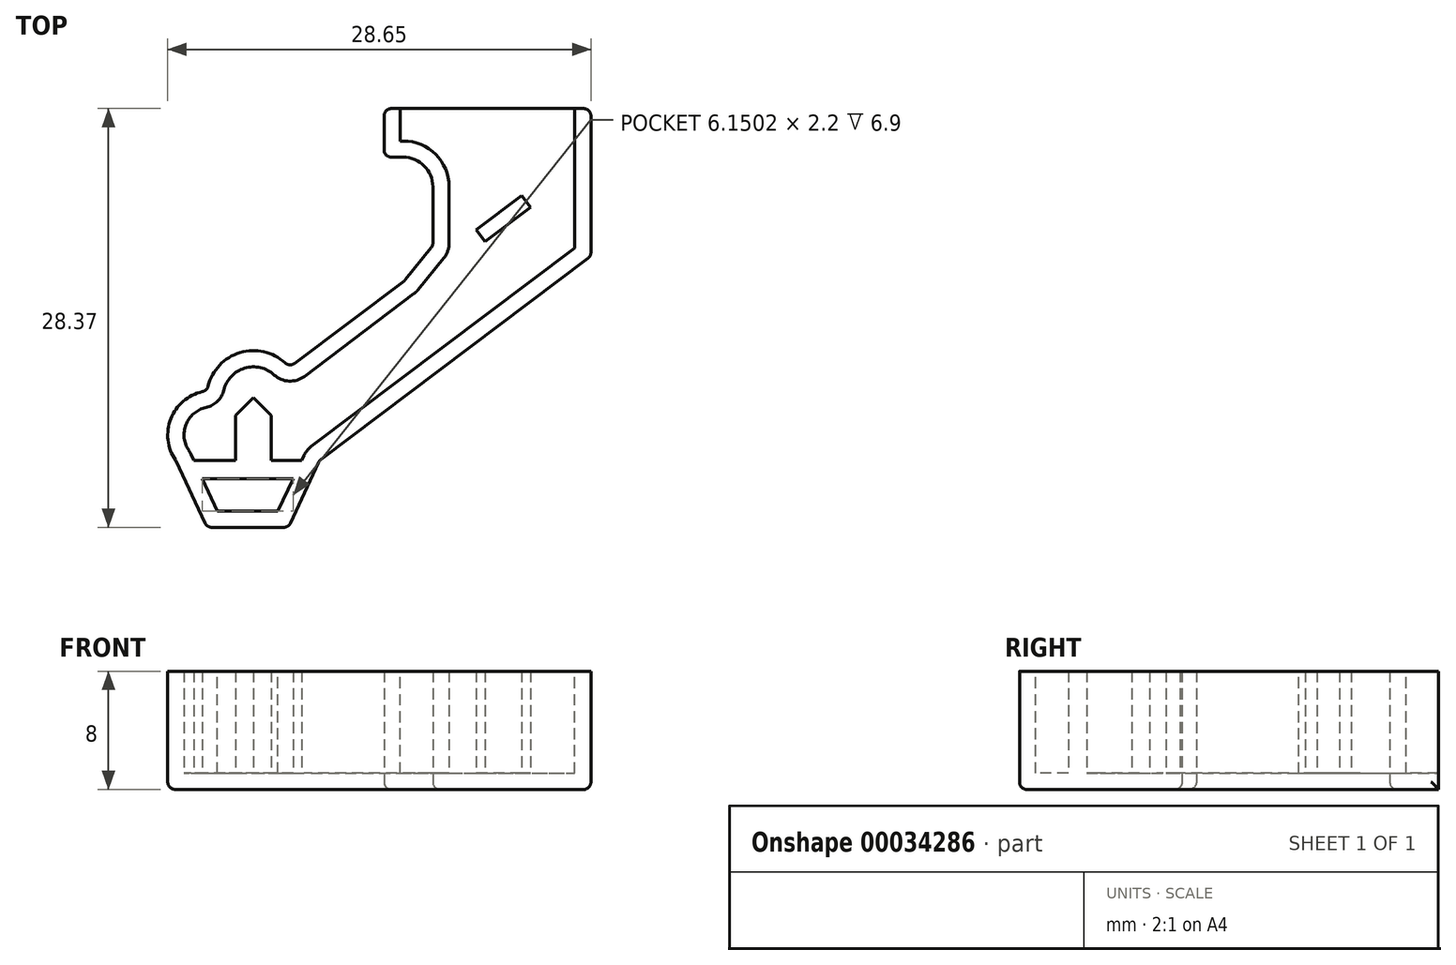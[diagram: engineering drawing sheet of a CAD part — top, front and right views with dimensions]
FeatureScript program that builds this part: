
annotation { "Feature Type Name" : "Feature", "Feature Type Description" : "" }
export const myFeature = defineFeature(function(context is Context, id is Id, definition is map)
    precondition{}
    {
        {
            var Q0;
            Q0=qCreatedBy(makeId("Top.planeOp"),FACE);
            var sketch = newSketch(context, id + "F0", { "sketchPlane" : qUnion([Q0])});
            skLineSegment(sketch, "E0", {"start": v(-14, 0) * mm, "end": v(0, 0) * mm});
            skLineSegment(sketch, "E1", {"start": v(0, 0) * mm, "end": v(0, -10) * mm});
            skLineSegment(sketch, "E2", {"start": v(0, -10) * mm, "end": v(-18.37, -23.84) * mm});
            skLineSegment(sketch, "E3", {"start": v(-18.37, -23.84) * mm, "end": v(-20.48, -28.37) * mm});
            skLineSegment(sketch, "E4", {"start": v(-20.48, -28.37) * mm, "end": v(-25.98, -28.37) * mm});
            skLineSegment(sketch, "E5", {"start": v(-25.98, -28.37) * mm, "end": v(-28.1, -23.84) * mm});
            skLineSegment(sketch, "E6", {"start": v(-14, 0) * mm, "end": v(-14, -3.3) * mm});
            skLineSegment(sketch, "E7", {"start": v(-14, -3.3) * mm, "end": v(-12.7, -3.3) * mm});
            skLineSegment(sketch, "E8", {"start": v(-10.7, -5.3) * mm, "end": v(-10.7, -9.3) * mm});
            skLineSegment(sketch, "E9", {"start": v(-10.7, -9.3) * mm, "end": v(-12.59, -11.63) * mm});
            skLineSegment(sketch, "E10", {"start": v(-12.59, -11.63) * mm, "end": v(-20.41, -17.53) * mm});
            skArc(sketch, "E11", {"start": v(-20.41, -17.53) * mm, "mid": v(-23.72, -16.52) * mm, "end": v(-25.98, -19.13) * mm});
            skArc(sketch, "E12", {"start": v(-25.98, -19.13) * mm, "mid": v(-28.39, -20.88) * mm, "end": v(-28.1, -23.84) * mm});
            skLineSegment(sketch, "E13", {"start": v(-25.98, -19.13) * mm, "end": v(-20.41, -17.53) * mm, "construction": true});
            skLineSegment(sketch, "E14", {"start": v(-25.98, -19.13) * mm, "end": v(-28.1, -23.84) * mm, "construction": true});
            skLineSegment(sketch, "E15", {"start": v(-25.98, -19.13) * mm, "end": v(-25.98, -28.37) * mm, "construction": true});
            skPoint(sketch, "E16.visualSharp", {"position": v(-10.7, -3.3) * mm});
            skArc(sketch, "E16.filletArc", {"start": v(-10.7, -5.3) * mm, "mid": v(-11.29, -3.89) * mm, "end": v(-12.7, -3.3) * mm});
            skSolve(sketch);
        }
        {
            var Q0;
            Q0 = qSketchRegion(id + "F0", true);
            extrude(context, id + "F1", {"entities" : qUnion([Q0]), "depth" : 8 * mm});
        }
        {
            var Q0;
            Q0=makeQuery(id+"F1.opExtrude","SWEPT_EDGE",EDGE,{"disambiguationData":[OSD([sQuery(id+"F0.wireOp",EDGE,"E6"),sQuery(id+"F0.wireOp",EDGE,"E7")])]});
            var Q1;
            Q1=makeQuery(id+"F1.opExtrude","SWEPT_EDGE",EDGE,{"disambiguationData":[OSD([sQuery(id+"F0.wireOp",EDGE,"E8"),sQuery(id+"F0.wireOp",EDGE,"E9")])]});
            var Q2;
            Q2=makeQuery(id+"F1.opExtrude","SWEPT_EDGE",EDGE,{"disambiguationData":[OSD([sQuery(id+"F0.wireOp",EDGE,"E9"),sQuery(id+"F0.wireOp",EDGE,"E10")])]});
            var Q3;
            Q3=makeQuery(id+"F1.opExtrude","SWEPT_EDGE",EDGE,{"disambiguationData":[OSD([sQuery(id+"F0.wireOp",EDGE,"E10"),sQuery(id+"F0.wireOp",EDGE,"E11")])]});
            var Q4;
            Q4=makeQuery(id+"F1.opExtrude","SWEPT_EDGE",EDGE,{"disambiguationData":[OSD([sQuery(id+"F0.wireOp",EDGE,"E11"),sQuery(id+"F0.wireOp",EDGE,"E12")])]});
            var Q5;
            Q5=makeQuery(id+"F1.opExtrude","SWEPT_EDGE",EDGE,{"disambiguationData":[OSD([sQuery(id+"F0.wireOp",EDGE,"E1"),sQuery(id+"F0.wireOp",EDGE,"E2")])]});
            var Q6;
            Q6=makeQuery(id+"F1.opExtrude","SWEPT_EDGE",EDGE,{"disambiguationData":[OSD([sQuery(id+"F0.wireOp",EDGE,"E2"),sQuery(id+"F0.wireOp",EDGE,"E3")])]});
            var Q7;
            Q7=makeQuery(id+"F1.opExtrude","SWEPT_EDGE",EDGE,{"disambiguationData":[OSD([sQuery(id+"F0.wireOp",EDGE,"E3"),sQuery(id+"F0.wireOp",EDGE,"E4")])]});
            var Q8;
            Q8=makeQuery(id+"F1.opExtrude","SWEPT_EDGE",EDGE,{"disambiguationData":[OSD([sQuery(id+"F0.wireOp",EDGE,"E4"),sQuery(id+"F0.wireOp",EDGE,"E5")])]});
            var Q9;
            Q9=makeQuery(id+"F1.opExtrude","SWEPT_EDGE",EDGE,{"disambiguationData":[OSD([sQuery(id+"F0.wireOp",EDGE,"E5"),sQuery(id+"F0.wireOp",EDGE,"E12")])]});
            var Q10;
            Q10=makeQuery(id+"F1.opExtrude","CAP_EDGE",EDGE,{"disambiguationData":[OSD([sQuery(id+"F0.wireOp",EDGE,"E4")])],"isStart":true});
            var Q11;
            Q11=makeQuery(id+"F1.opExtrude","CAP_EDGE",EDGE,{"disambiguationData":[OSD([sQuery(id+"F0.wireOp",EDGE,"E5")])],"isStart":true});
            var Q12;
            Q12=makeQuery(id+"F1.opExtrude","CAP_EDGE",EDGE,{"disambiguationData":[OSD([sQuery(id+"F0.wireOp",EDGE,"E12")])],"isStart":true});
            var Q13;
            Q13=makeQuery(id+"F1.opExtrude","CAP_EDGE",EDGE,{"disambiguationData":[OSD([sQuery(id+"F0.wireOp",EDGE,"E11")])],"isStart":true});
            var Q14;
            Q14=makeQuery(id+"F1.opExtrude","CAP_EDGE",EDGE,{"disambiguationData":[OSD([sQuery(id+"F0.wireOp",EDGE,"E10")])],"isStart":true});
            var Q15;
            Q15=makeQuery(id+"F1.opExtrude","CAP_EDGE",EDGE,{"disambiguationData":[OSD([sQuery(id+"F0.wireOp",EDGE,"E9")])],"isStart":true});
            var Q16;
            Q16=makeQuery(id+"F1.opExtrude","CAP_EDGE",EDGE,{"disambiguationData":[OSD([sQuery(id+"F0.wireOp",EDGE,"E8")])],"isStart":true});
            var Q17;
            Q17=makeQuery(id+"F1.opExtrude","CAP_EDGE",EDGE,{"disambiguationData":[OSD([sQuery(id+"F0.wireOp",EDGE,"E7")])],"isStart":true});
            var Q18;
            Q18=makeQuery(id+"F1.opExtrude","CAP_EDGE",EDGE,{"disambiguationData":[OSD([sQuery(id+"F0.wireOp",EDGE,"E6")])],"isStart":true});
            var Q19;
            Q19=makeQuery(id+"F1.opExtrude","CAP_EDGE",EDGE,{"disambiguationData":[OSD([sQuery(id+"F0.wireOp",EDGE,"E1")])],"isStart":true});
            var Q20;
            Q20=makeQuery(id+"F1.opExtrude","CAP_EDGE",EDGE,{"disambiguationData":[OSD([sQuery(id+"F0.wireOp",EDGE,"E2")])],"isStart":true});
            var Q21;
            Q21=makeQuery(id+"F1.opExtrude","CAP_EDGE",EDGE,{"disambiguationData":[OSD([sQuery(id+"F0.wireOp",EDGE,"E3")])],"isStart":true});
            var Q22;
            Q22=makeQuery(id+"F1.opExtrude","SWEPT_EDGE",EDGE,{"disambiguationData":[OSD([sQuery(id+"F0.wireOp",EDGE,"E0"),sQuery(id+"F0.wireOp",EDGE,"E1")])]});
            var Q23;
            Q23=makeQuery(id+"F1.opExtrude","SWEPT_EDGE",EDGE,{"disambiguationData":[OSD([sQuery(id+"F0.wireOp",EDGE,"E0"),sQuery(id+"F0.wireOp",EDGE,"E6")])]});
            fillet(context, id + "F2", {"entities" : qUnion([Q0, Q1, Q2, Q3, Q4, Q5, Q6, Q7, Q8, Q9, Q10, Q11, Q12, Q13, Q14, Q15, Q16, Q17, Q18, Q19, Q20, Q21, Q22, Q23]), "radius" : .5 * mm, "allowEdgeOverflow" : false});
        }
        {
            var Q0;
            Q0=makeQuery(id+"F1.opExtrude","CAP_FACE",FACE,{"disambiguationData":[OSD([sQuery(id+"F0.wireOp",EDGE,"E0"),sQuery(id+"F0.wireOp",EDGE,"E1"),sQuery(id+"F0.wireOp",EDGE,"E2"),sQuery(id+"F0.wireOp",EDGE,"E3"),sQuery(id+"F0.wireOp",EDGE,"E4"),sQuery(id+"F0.wireOp",EDGE,"E5"),sQuery(id+"F0.wireOp",EDGE,"E6"),sQuery(id+"F0.wireOp",EDGE,"E7"),sQuery(id+"F0.wireOp",EDGE,"E8"),sQuery(id+"F0.wireOp",EDGE,"E9"),sQuery(id+"F0.wireOp",EDGE,"E10"),sQuery(id+"F0.wireOp",EDGE,"E11"),sQuery(id+"F0.wireOp",EDGE,"E12")])],"isStart":false});
            var Q1;
            Q1=makeQuery(id+"F1.opExtrude","SWEPT_FACE",FACE,{"disambiguationData":[OSD([sQuery(id+"F0.wireOp",EDGE,"E0")])]});
            shell(context, id + "F3", {"entities" : qUnion([Q0, Q1]), "thickness" : 1.1 * mm});
        }
        {
            var Q0;
            Q0=makeQuery(id+"F3.opShell","OFFSET_FACE",FACE,{"disambiguationData":[OSD([sQuery(id+"F0.wireOp",EDGE,"E0"),sQuery(id+"F0.wireOp",EDGE,"E1"),sQuery(id+"F0.wireOp",EDGE,"E2"),sQuery(id+"F0.wireOp",EDGE,"E3"),sQuery(id+"F0.wireOp",EDGE,"E4"),sQuery(id+"F0.wireOp",EDGE,"E5"),sQuery(id+"F0.wireOp",EDGE,"E6"),sQuery(id+"F0.wireOp",EDGE,"E7"),sQuery(id+"F0.wireOp",EDGE,"E8"),sQuery(id+"F0.wireOp",EDGE,"E9"),sQuery(id+"F0.wireOp",EDGE,"E10"),sQuery(id+"F0.wireOp",EDGE,"E11"),sQuery(id+"F0.wireOp",EDGE,"E12")])]});
            var sketch = newSketch(context, id + "F4", { "sketchPlane" : qUnion([Q0])});
            skLineSegment(sketch, "E17", {"start": v(-26.89, -23.82) * mm, "end": v(-24.04, -23.82) * mm});
            skLineSegment(sketch, "E18", {"start": v(-20.16, -25.07) * mm, "end": v(-26.3, -25.07) * mm});
            skLineSegment(sketch, "E19", {"start": v(-24.04, -23.82) * mm, "end": v(-24.04, -20.77) * mm});
            skLineSegment(sketch, "E20", {"start": v(-24.04, -20.77) * mm, "end": v(-22.84, -19.57) * mm});
            skLineSegment(sketch, "E21", {"start": v(-22.84, -19.57) * mm, "end": v(-21.64, -20.77) * mm});
            skLineSegment(sketch, "E22", {"start": v(-21.64, -20.77) * mm, "end": v(-21.64, -23.82) * mm});
            skLineSegment(sketch, "E23.trimOffspring", {"start": v(-21.64, -23.82) * mm, "end": v(-19.57, -23.82) * mm});
            skLineSegment(sketch, "E24", {"start": v(-24.04, -20.77) * mm, "end": v(-21.64, -20.77) * mm, "construction": true});
            skLineSegment(sketch, "E25", {"start": v(-7.17, -9.02) * mm, "end": v(-4.1, -6.7) * mm});
            skLineSegment(sketch, "E26", {"start": v(-4.1, -6.7) * mm, "end": v(-4.7, -5.9) * mm});
            skLineSegment(sketch, "E27", {"start": v(-4.7, -5.9) * mm, "end": v(-7.78, -8.22) * mm});
            skLineSegment(sketch, "E28", {"start": v(-7.78, -8.22) * mm, "end": v(-7.17, -9.02) * mm});
            skLineSegment(sketch, "E29", {"start": v(-22.84, -19.57) * mm, "end": v(-22.84, -17.5) * mm, "construction": true});
            skLineSegment(sketch, "E30", {"start": v(-22.84, -17.5) * mm, "end": v(-28.48, -17.5) * mm, "construction": true});
            skLineSegment(sketch, "E31", {"start": v(-26.89, -23.82) * mm, "end": v(-26.3, -25.07) * mm});
            skLineSegment(sketch, "E32", {"start": v(-19.57, -23.82) * mm, "end": v(-20.16, -25.07) * mm});
            skSolve(sketch);
        }
        {
            var Q0;
            Q0 = qSketchRegion(id + "F4", true);
            var Q1;
            Q1=makeQuery(id+"F1.opExtrude","CAP_FACE",FACE,{"disambiguationData":[OSD([sQuery(id+"F0.wireOp",EDGE,"E0"),sQuery(id+"F0.wireOp",EDGE,"E1"),sQuery(id+"F0.wireOp",EDGE,"E2"),sQuery(id+"F0.wireOp",EDGE,"E3"),sQuery(id+"F0.wireOp",EDGE,"E4"),sQuery(id+"F0.wireOp",EDGE,"E5"),sQuery(id+"F0.wireOp",EDGE,"E6"),sQuery(id+"F0.wireOp",EDGE,"E7"),sQuery(id+"F0.wireOp",EDGE,"E8"),sQuery(id+"F0.wireOp",EDGE,"E9"),sQuery(id+"F0.wireOp",EDGE,"E10"),sQuery(id+"F0.wireOp",EDGE,"E11"),sQuery(id+"F0.wireOp",EDGE,"E12")])],"isStart":false});
            extrude(context, id + "F5", {"entities" : qUnion([Q0]), "operationType" : NewBodyOperationType.ADD, "endBound" : BoundingType.UP_TO_SURFACE, "endBoundEntityFace" : qUnion([Q1]), "depth" : 25 * mm});
        }
    });
